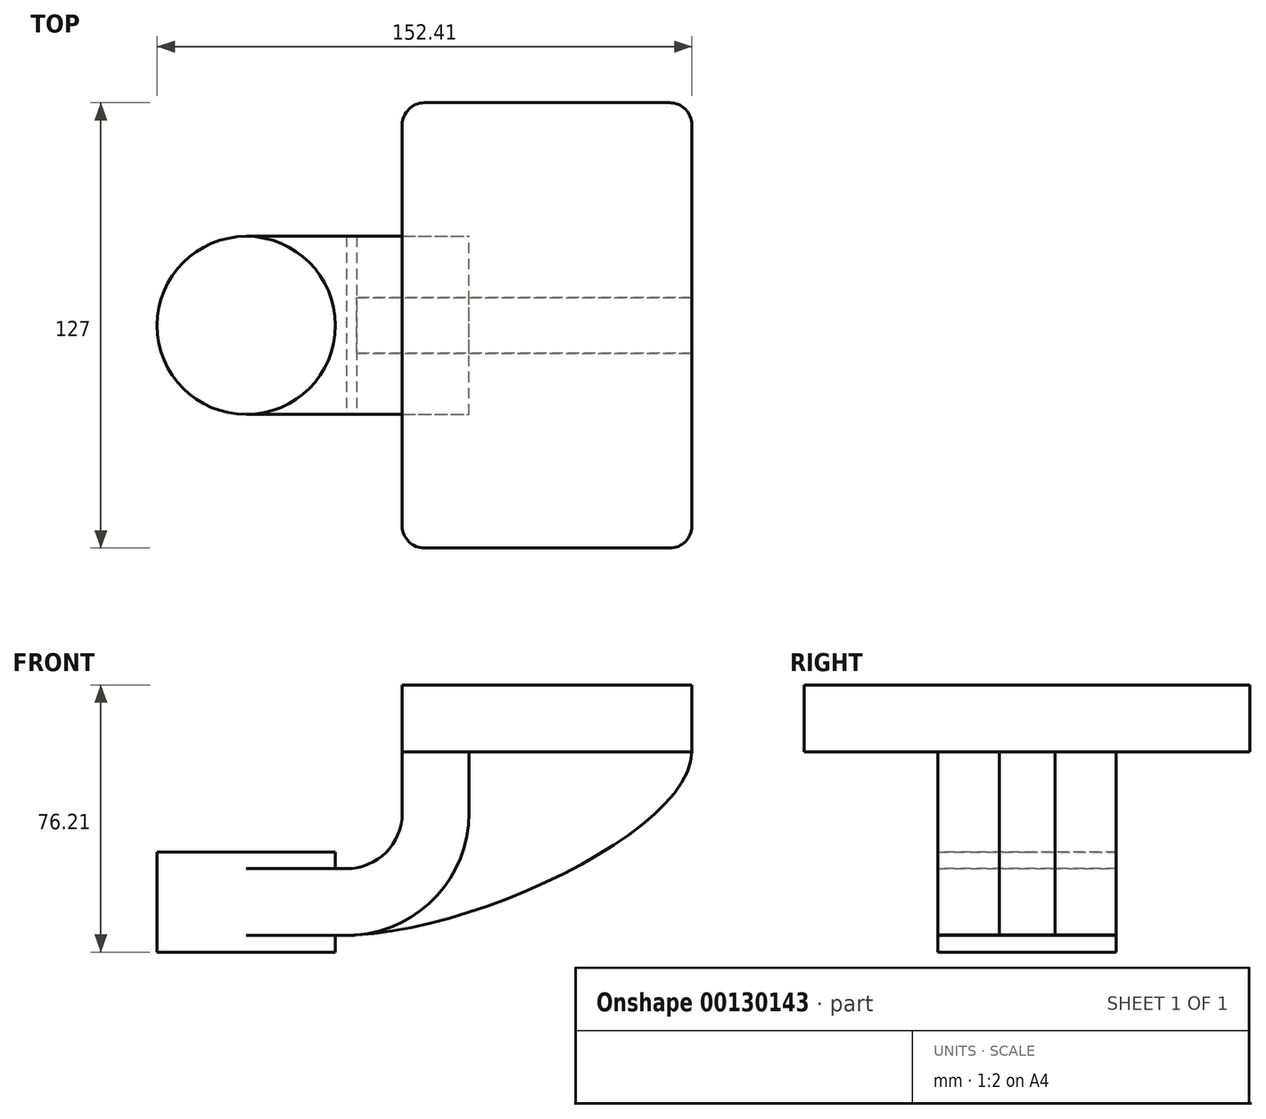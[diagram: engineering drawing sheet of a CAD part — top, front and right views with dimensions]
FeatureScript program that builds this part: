
annotation { "Feature Type Name" : "Feature", "Feature Type Description" : "" }
export const myFeature = defineFeature(function(context is Context, id is Id, definition is map)
    precondition{}
    {
        {
            var Q0;
            Q0=qCreatedBy(makeId("Front.planeOp"),FACE);
            var sketch = newSketch(context, id + "F0", { "sketchPlane" : qUnion([Q0])});
            skLineSegment(sketch, "E0.bottom", {"start": v(-41.28, -9.52) * mm, "end": v(41.28, -9.52) * mm});
            skLineSegment(sketch, "E0.top", {"start": v(-41.28, 9.53) * mm, "end": v(41.28, 9.53) * mm});
            skLineSegment(sketch, "E0.left", {"start": v(-41.28, -9.53) * mm, "end": v(-41.28, 9.53) * mm});
            skLineSegment(sketch, "E0.right", {"start": v(41.28, -9.53) * mm, "end": v(41.28, 9.53) * mm});
            skPoint(sketch, "E0.middle", {"position": v(0, 0) * mm});
            skLineSegment(sketch, "E1.bottom", {"start": v(-60.33, -38.1) * mm, "end": v(-111.12, -38.1) * mm});
            skLineSegment(sketch, "E1.top", {"start": v(-60.33, -66.68) * mm, "end": v(-111.12, -66.68) * mm});
            skLineSegment(sketch, "E1.left", {"start": v(-60.33, -38.1) * mm, "end": v(-60.32, -66.67) * mm});
            skLineSegment(sketch, "E1.right", {"start": v(-111.12, -38.1) * mm, "end": v(-111.12, -66.67) * mm});
            skPoint(sketch, "E1.middle", {"position": v(-85.72, -52.39) * mm});
            skLineSegment(sketch, "E2", {"start": v(-41.28, -9.53) * mm, "end": v(-41.28, -27) * mm});
            skArc(sketch, "E3", {"start": v(-41.28, -27) * mm, "mid": v(-45.92, -38.23) * mm, "end": v(-57.15, -42.88) * mm});
            skLineSegment(sketch, "E4", {"start": v(-57.15, -42.88) * mm, "end": v(-85.72, -42.88) * mm});
            skLineSegment(sketch, "E5.0", {"start": v(-57.15, -61.93) * mm, "end": v(-85.72, -61.93) * mm});
            skArc(sketch, "E5.1", {"start": v(-22.23, -27) * mm, "mid": v(-32.45, -51.7) * mm, "end": v(-57.15, -61.93) * mm});
            skLineSegment(sketch, "E5.2", {"start": v(-22.23, -9.53) * mm, "end": v(-22.23, -27) * mm});
            skFitSpline(sketch, "E6", {"points": [v(41.27, -9.52) * mm, v(-57.15, -61.93) * mm], "startDerivative": vector(-0.96, -67.22) * mm, "endDerivative": vector(-110.1, -2.44) * mm});
            skLineSegment(sketch, "E7", {"start": v(-85.72, -66.68) * mm, "end": v(-85.72, -38.1) * mm});
            skSolve(sketch);
        }
        {
            var Q0;
            Q0=makeQuery(id+"F0.imprint","IMPRINT",FACE,{"disambiguationData":[TD([[makeQuery(id+"F0.imprint","IMPRINT",EDGE,{"derivedFrom":sQuery(id+"F0.wireOp",EDGE,"E0.top")}),-1.0]])]});
            extrude(context, id + "F1", {"entities" : qUnion([Q0]), "endBound" : BoundingType.SYMMETRIC, "depth" : 127 * mm});
        }
        {
            var Q0;
            {var subQ1=sQuery(id+"F0.wireOp",EDGE,"E2");Q0=makeQuery(id+"F0.imprint","IMPRINT",FACE,{"disambiguationData":[TD([[makeQuery(id+"F0.imprint","IMPRINT",EDGE,{"derivedFrom":subQ1}),1.0]])]});}
            extrude(context, id + "F2", {"entities" : qUnion([Q0]), "endBound" : BoundingType.SYMMETRIC, "depth" : 50.8 * mm});
        }
        {
            var Q0;
            {var subQ0=sQuery(id+"F0.wireOp",EDGE,"E4");var subQ1=sQuery(id+"F0.wireOp",EDGE,"E1.left");var subQ2=makeQuery(id+"F0.imprint","INTERSECT",VERTEX,{"derivedFrom":[subQ1,subQ0]});Q0=makeQuery(id+"F0.imprint","IMPRINT",FACE,{"disambiguationData":[TD([[makeQuery(id+"F0.imprint","IMPRINT",EDGE,{"disambiguationData":[TD([[subQ2,-1.0]])],"derivedFrom":subQ1}),-1.0]])]});}
            extrude(context, id + "F3", {"entities" : qUnion([Q0]), "operationType" : NewBodyOperationType.ADD, "endBound" : BoundingType.SYMMETRIC, "depth" : 50.8 * mm});
        }
        {
            var Q0;
            {var subQ3=sQuery(id+"F0.wireOp",EDGE,"E5.2");Q0=makeQuery(id+"F0.imprint","IMPRINT",FACE,{"disambiguationData":[TD([[makeQuery(id+"F0.imprint","IMPRINT",EDGE,{"derivedFrom":subQ3}),1.0]])]});}
            extrude(context, id + "F4", {"entities" : qUnion([Q0]), "endBound" : BoundingType.SYMMETRIC, "depth" : 15.88 * mm});
        }
        {
            var Q0;
            {var subQ0=sQuery(id+"F0.wireOp",EDGE,"E1.right");Q0=makeQuery(id+"F0.imprint","IMPRINT",FACE,{"disambiguationData":[TD([[makeQuery(id+"F0.imprint","IMPRINT",EDGE,{"derivedFrom":subQ0}),1.0]])]});}
            var Q1;
            Q1=sQuery(id+"F0.wireOp",EDGE,"E7");
            revolve(context, id + "F5", {"operationType" : NewBodyOperationType.ADD, "entities" : qUnion([Q0]), "axis" : qUnion([Q1]), "revolveType" : RevolveType.FULL});
        }
        {
            var Q0;
            Q0=makeQuery(id+"F1.opExtrude","CAP_EDGE",EDGE,{"disambiguationData":[OSD([sQuery(id+"F0.wireOp",EDGE,"E0.right")])],"isStart":false});
            var Q1;
            Q1=makeQuery(id+"F1.opExtrude","CAP_EDGE",EDGE,{"disambiguationData":[OSD([sQuery(id+"F0.wireOp",EDGE,"E0.left")])],"isStart":false});
            var Q2;
            Q2=makeQuery(id+"F1.opExtrude","CAP_EDGE",EDGE,{"disambiguationData":[OSD([sQuery(id+"F0.wireOp",EDGE,"E0.left")])],"isStart":true});
            var Q3;
            Q3=makeQuery(id+"F1.opExtrude","CAP_EDGE",EDGE,{"disambiguationData":[OSD([sQuery(id+"F0.wireOp",EDGE,"E0.right")])],"isStart":true});
            fillet(context, id + "F6", {"entities" : qUnion([Q0, Q1, Q2, Q3]), "radius" : 6.35 * mm, "tangentPropagation" : true, "allowEdgeOverflow" : false});
        }
    });
